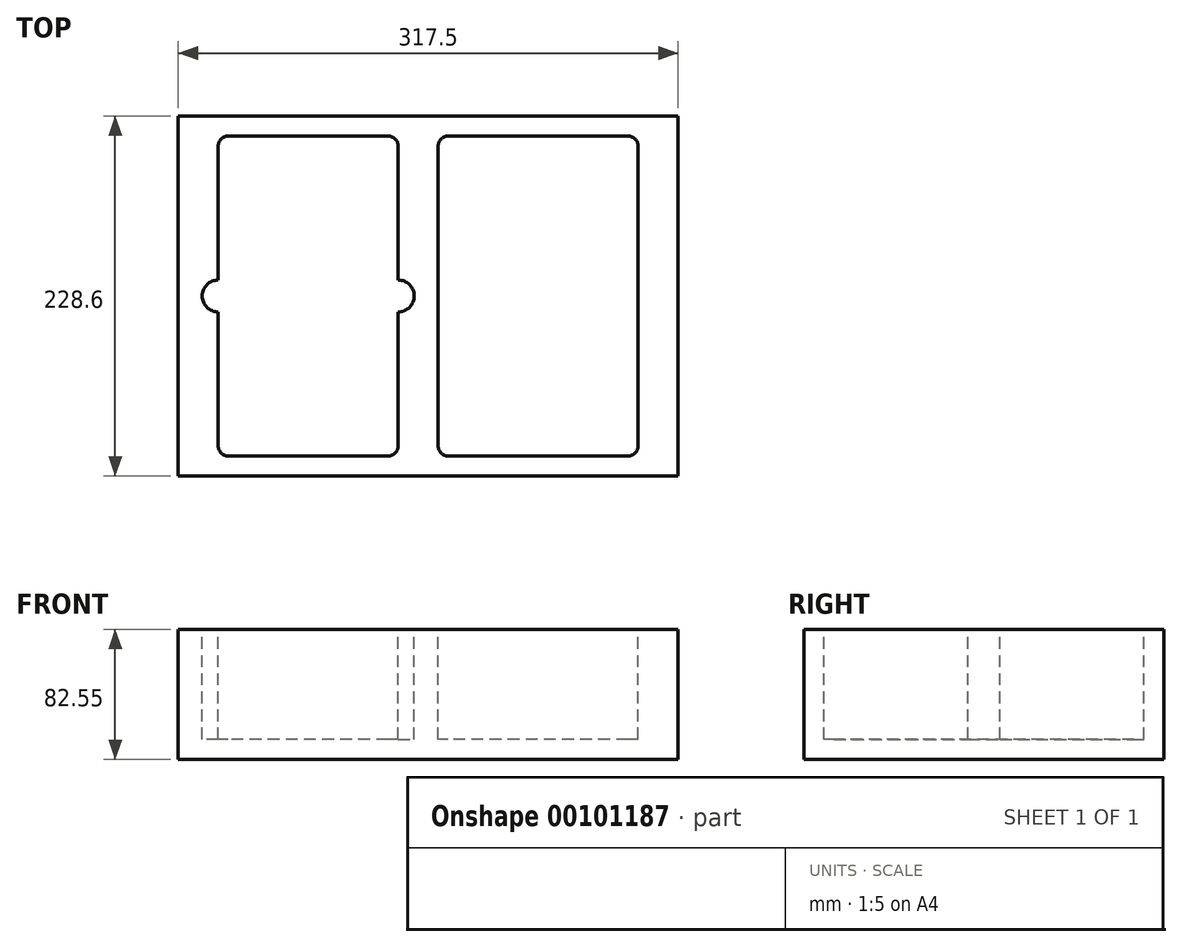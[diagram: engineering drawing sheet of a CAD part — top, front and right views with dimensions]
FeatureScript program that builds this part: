
annotation { "Feature Type Name" : "Feature", "Feature Type Description" : "" }
export const myFeature = defineFeature(function(context is Context, id is Id, definition is map)
    precondition{}
    {
        {
            var Q0;
            Q0=qCreatedBy(makeId("Top.planeOp"),FACE);
            var sketch = newSketch(context, id + "F0", { "sketchPlane" : qUnion([Q0])});
            skLineSegment(sketch, "E0.bottom", {"start": v(158.75, 114.3) * mm, "end": v(-158.75, 114.3) * mm});
            skLineSegment(sketch, "E0.top", {"start": v(158.75, -114.3) * mm, "end": v(-158.75, -114.3) * mm});
            skLineSegment(sketch, "E0.left", {"start": v(158.75, 114.3) * mm, "end": v(158.75, -114.3) * mm});
            skLineSegment(sketch, "E0.right", {"start": v(-158.75, 114.3) * mm, "end": v(-158.75, -114.3) * mm});
            skPoint(sketch, "E0.middle", {"position": v(0, 0) * mm});
            skSolve(sketch);
        }
        {
            var Q0;
            Q0=makeQuery(id+"F0.imprint","IMPRINT",FACE,{"disambiguationData":[TD([[makeQuery(id+"F0.imprint","IMPRINT",EDGE,{"derivedFrom":sQuery(id+"F0.wireOp",EDGE,"E0.bottom")}),1.0]])]});
            extrude(context, id + "F1", {"entities" : qUnion([Q0]), "depth" : 82.55 * mm});
        }
        {
            var Q0;
            Q0=makeQuery(id+"F1.opExtrude","CAP_FACE",FACE,{"disambiguationData":[OSD([sQuery(id+"F0.wireOp",EDGE,"E0.bottom"),sQuery(id+"F0.wireOp",EDGE,"E0.top"),sQuery(id+"F0.wireOp",EDGE,"E0.left"),sQuery(id+"F0.wireOp",EDGE,"E0.right")])],"isStart":false});
            var sketch = newSketch(context, id + "F2", { "sketchPlane" : qUnion([Q0])});
            skLineSegment(sketch, "E1.bottom", {"start": v(-25.4, -101.6) * mm, "end": v(-127, -101.6) * mm});
            skLineSegment(sketch, "E1.top", {"start": v(-25.4, 101.6) * mm, "end": v(-127, 101.6) * mm});
            skLineSegment(sketch, "E1.left", {"start": v(-19.05, -95.25) * mm, "end": v(-19.05, 95.25) * mm});
            skLineSegment(sketch, "E1.right", {"start": v(-133.35, -95.25) * mm, "end": v(-133.35, 95.25) * mm});
            skPoint(sketch, "E1.middle", {"position": v(-76.2, 0) * mm});
            skLineSegment(sketch, "E2.bottom", {"start": v(127, 101.6) * mm, "end": v(12.7, 101.6) * mm});
            skLineSegment(sketch, "E2.top", {"start": v(127, -101.6) * mm, "end": v(12.7, -101.6) * mm});
            skLineSegment(sketch, "E2.left", {"start": v(133.35, 95.25) * mm, "end": v(133.35, -95.25) * mm});
            skLineSegment(sketch, "E2.right", {"start": v(6.35, 95.25) * mm, "end": v(6.35, -95.25) * mm});
            skPoint(sketch, "E2.middle", {"position": v(69.85, 0) * mm});
            skPoint(sketch, "E3.visualSharp", {"position": v(-19.05, 101.6) * mm});
            skArc(sketch, "E3.filletArc", {"start": v(-19.05, 95.25) * mm, "mid": v(-20.9, 99.74) * mm, "end": v(-25.4, 101.6) * mm});
            skPoint(sketch, "E4.visualSharp", {"position": v(-19.05, -101.6) * mm});
            skArc(sketch, "E4.filletArc", {"start": v(-25.4, -101.6) * mm, "mid": v(-20.9, -99.74) * mm, "end": v(-19.05, -95.25) * mm});
            skPoint(sketch, "E5.visualSharp", {"position": v(-133.35, -101.6) * mm});
            skArc(sketch, "E5.filletArc", {"start": v(-133.35, -95.25) * mm, "mid": v(-131.5, -99.74) * mm, "end": v(-127, -101.6) * mm});
            skPoint(sketch, "E6.visualSharp", {"position": v(-133.35, 101.6) * mm});
            skArc(sketch, "E6.filletArc", {"start": v(-127, 101.6) * mm, "mid": v(-131.5, 99.74) * mm, "end": v(-133.35, 95.25) * mm});
            skPoint(sketch, "E7.visualSharp", {"position": v(6.35, 101.6) * mm});
            skArc(sketch, "E7.filletArc", {"start": v(12.7, 101.6) * mm, "mid": v(8.2, 99.74) * mm, "end": v(6.35, 95.25) * mm});
            skPoint(sketch, "E8.visualSharp", {"position": v(133.35, 101.6) * mm});
            skArc(sketch, "E8.filletArc", {"start": v(133.35, 95.25) * mm, "mid": v(131.5, 99.74) * mm, "end": v(127, 101.6) * mm});
            skPoint(sketch, "E9.visualSharp", {"position": v(133.35, -101.6) * mm});
            skArc(sketch, "E9.filletArc", {"start": v(127, -101.6) * mm, "mid": v(131.5, -99.74) * mm, "end": v(133.35, -95.25) * mm});
            skPoint(sketch, "E10.visualSharp", {"position": v(6.35, -101.6) * mm});
            skArc(sketch, "E10.filletArc", {"start": v(6.35, -95.25) * mm, "mid": v(8.2, -99.74) * mm, "end": v(12.7, -101.6) * mm});
            skCircle(sketch, "E11", {"center": v(-19.05, 0) * mm, "radius": 10.16 * mm});
            skCircle(sketch, "E12", {"center": v(-133.35, 0) * mm, "radius": 10.16 * mm});
            skSolve(sketch);
        }
        {
            var Q0;
            Q0 = qSketchRegion(id + "F2", true);
            extrude(context, id + "F3", {"entities" : qUnion([Q0]), "operationType" : NewBodyOperationType.REMOVE, "oppositeDirection" : true, "depth" : 69.85 * mm});
        }
    });
